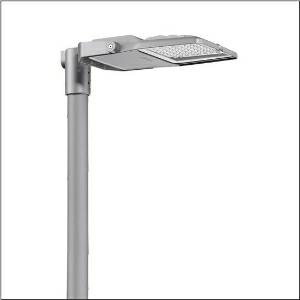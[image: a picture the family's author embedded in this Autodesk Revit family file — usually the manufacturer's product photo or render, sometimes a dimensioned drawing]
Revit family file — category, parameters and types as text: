
# Revit family: floodlight_fl_21_mini___pl33t_5xa7775d2f3a_2fb5
name_source: partatom
category: Lighting Fixtures
units: mm (PartAtom-declared; Revit-internal decimal feet)

## family parameters
Cut with Voids When Loaded = No
Host = Face
Light Source = No
Part Type = Normal
Room Calculation Point = No
Round Connector Dimension = Use Diameter
Shared = No

## types (1)
- --- (1 x LED, 17630 lm, 142.9 W, 3000K)
    Apparent Load = 143 VA
    CIE Flux Codes = 26 75 99 100 100
    Color Rendering = 70
    Color Temperature = 3000K
    Default Elevation = 1800 mm
    Description = Floodlight FL 21 mini, floodlight, primary light control with lens, of PMMA, primary optical cover: protective disc, of toughened safety glass, transparent, light distribution: PL33T, light emission: direct distribution, installation type: surface-mounted, LED, High Power LED, rated luminous flux: 17.630lm, luminous efficacy: 123lm/W, light colour: 730, colour temperature: 3000K, control gear: Smart Interface (Zhaga), control: flexible luminous flux parameterisation, time-dependent luminous flux control, constant luminous flux control, overheat protection, pre-setting: logarithmic dimming characteristic, with terminal, 6-pole, mains connection: 220..240V, AC, 50/60Hz, start of lifetime: 143W, end of service life: 151W, reduction: 63W, luminaire housing, of diecast aluminium, powder-coated, Siteco® metallic grey (DB 702S), corrosivity category C5 mid according to DIN EN ISO 12944, suitable for swimming pools, chlorine-resistant, sealing non-destructively replaceable, please order mast flange separately, mast bracket, of steel, galvanised, powder-coated, Siteco® metallic grey (DB 702S), Smart Interface above, protection rating (complete): IP66, insulation class (complete): insulation class II (safety insulation), certification: CE, ENEC, VDE, protection symbol: D, impact resistance: IK08, permissible operating ambient temperature: -40..+40°C, permissible operating ambient temperature for outdoor applications: -40..+50°C, standard: DIN EN 12944, LABS conformity tested according to VDMA 24364:2018-05, packaging unit: 1 piece

Light Distribution: PL33T
    Height = 70 mm
    Lamp = 1 x LED
    Lamp Light Flux = 17630 lm
    Lamp Power = 142.9 W
    Lamp count = 1
    Length = 485 mm
    Luminous efficacy = 123 lm/W
    Manufacturer = Siteco
    ModVariant = No
    Model = 5XA7775D2F3A
    Number of Poles = 1
    OnlyDefault = Yes
    Power Factor = 1
    Product Name = Floodlight FL 21 mini | PL33T
    Product group = floodlight | pylon annexe
    ProductGroupID = 6200
    Protection Class = Protection class II
    Protection Degree = IP 66
    RLX_Detail_Level = 1
    RLX_Emergency_Light_Flux = 0 lm
    RLX_Emergency_Type = 0
    RLX_Emergency_Type_DB = No
    RlxData = <blob elided: 101417 chars, md5=eb09eb4e>
    Socket = socket
    Standby Power = 0 W
    System Light Flux = 17630 lm
    System Power = 143 W
    Type Comments = factory setting: luminous flux: 100 % | dim-lin: 254 | 730 mA
    Type Image = l_1007125.jpg
    URL = http://relux.com
    VarID = @adj_148406
    Voltage = 0 V
    Weight = 0.00 kg
    Width = 337 mm

## geometry (parser evidence)
native form markers: Blend x4, Sweep x11
no freeform markers — native parametric forms only
